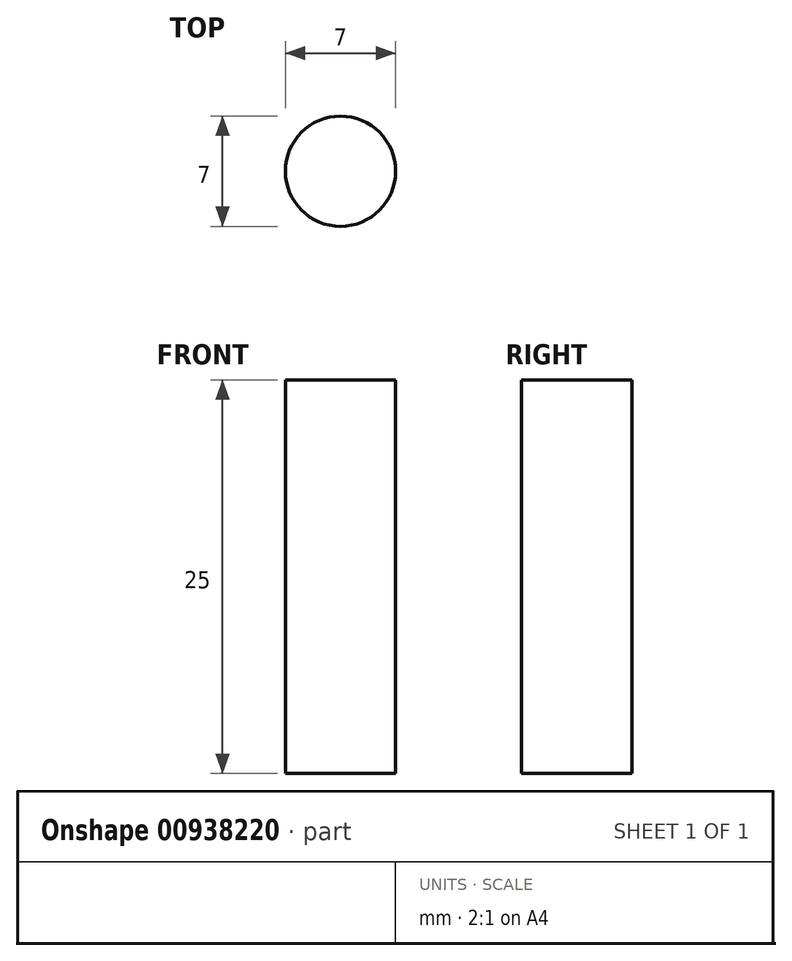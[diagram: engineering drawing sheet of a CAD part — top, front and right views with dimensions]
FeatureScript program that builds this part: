
annotation { "Feature Type Name" : "Feature", "Feature Type Description" : "" }
export const myFeature = defineFeature(function(context is Context, id is Id, definition is map)
    precondition{}
    {
        {
            var Q0;
            Q0=qCreatedBy(makeId("Top.planeOp"),FACE);
            var sketch = newSketch(context, id + "F0", { "sketchPlane" : qUnion([Q0])});
            skCircle(sketch, "E0", {"center": v(0, 0) * mm, "radius": 3.5 * mm});
            skSolve(sketch);
        }
        {
            var Q0;
            Q0=makeQuery(id+"F0.imprint","IMPRINT",FACE,{"disambiguationData":[TD([[makeQuery(id+"F0.imprint","IMPRINT",EDGE,{"derivedFrom":sQuery(id+"F0.wireOp",EDGE,"E0")}),1.0]])]});
            extrude(context, id + "F1", {"entities" : qUnion([Q0]), "depth" : 25 * mm, "offsetDistance" : 25 * mm});
        }
    });
